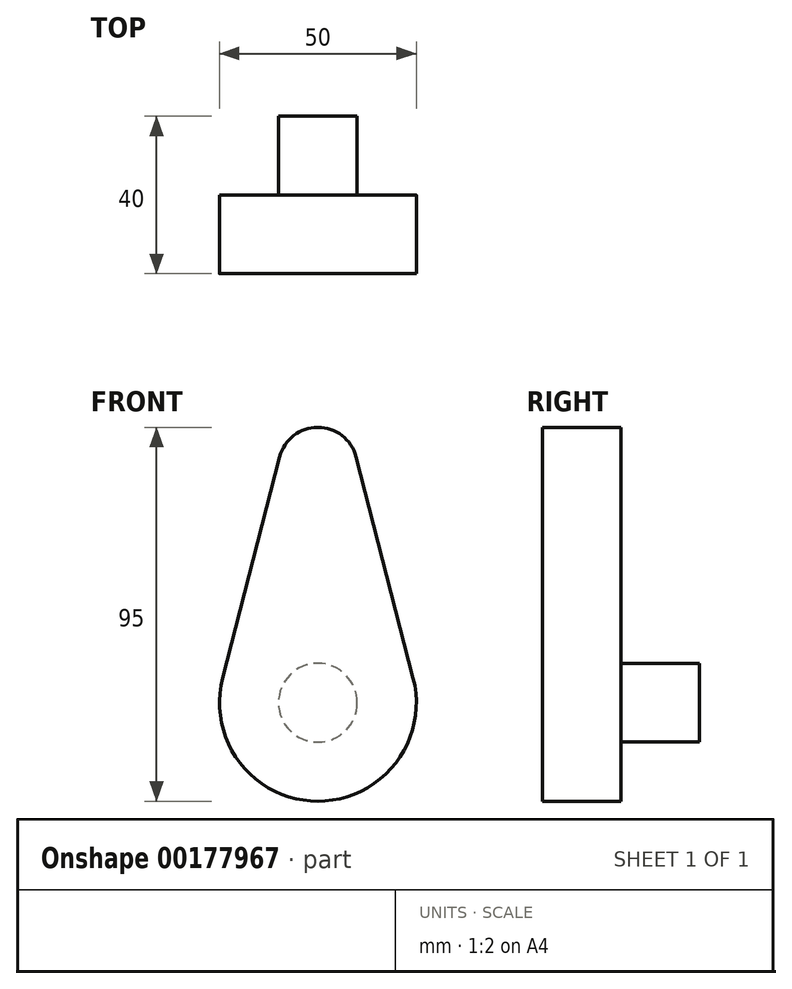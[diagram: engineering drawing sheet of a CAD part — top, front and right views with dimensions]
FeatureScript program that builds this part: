
annotation { "Feature Type Name" : "Feature", "Feature Type Description" : "" }
export const myFeature = defineFeature(function(context is Context, id is Id, definition is map)
    precondition{}
    {
        {
            var Q0;
            Q0=qCreatedBy(makeId("Front.planeOp"),FACE);
            var sketch = newSketch(context, id + "F0", { "sketchPlane" : qUnion([Q0])});
            skCircle(sketch, "E0", {"center": v(0, 0) * mm, "radius": 25 * mm});
            skCircle(sketch, "E1", {"center": v(0, 60) * mm, "radius": 10 * mm});
            skLineSegment(sketch, "E2", {"start": v(0, 60) * mm, "end": v(0, 0) * mm, "construction": true});
            skLineSegment(sketch, "E3", {"start": v(-9.68, 62.5) * mm, "end": v(-24.2, 6.25) * mm});
            skLineSegment(sketch, "E4.MirrorCS", {"start": v(9.68, 62.5) * mm, "end": v(24.2, 6.25) * mm});
            skSolve(sketch);
        }
        {
            var Q0;
            {var subQ0=sQuery(id+"F0.wireOp",EDGE,"E0");var subQ1=makeQuery(id+"F0.imprint","INTERSECT",VERTEX,{"derivedFrom":[subQ0,sQuery(id+"F0.wireOp",EDGE,"E3")]});Q0=makeQuery(id+"F0.imprint","IMPRINT",FACE,{"disambiguationData":[TD([[makeQuery(id+"F0.imprint","IMPRINT",EDGE,{"disambiguationData":[TD([[subQ1,1.0]])],"derivedFrom":subQ0}),1.0]])]});}
            var Q1;
            {var subQ0=sQuery(id+"F0.wireOp",EDGE,"E1");var subQ1=makeQuery(id+"F0.imprint","INTERSECT",VERTEX,{"derivedFrom":[subQ0,sQuery(id+"F0.wireOp",EDGE,"E3")]});Q1=makeQuery(id+"F0.imprint","IMPRINT",FACE,{"disambiguationData":[TD([[makeQuery(id+"F0.imprint","IMPRINT",EDGE,{"disambiguationData":[TD([[subQ1,1.0]])],"derivedFrom":subQ0}),1.0]])]});}
            var Q2;
            {var subQ0=sQuery(id+"F0.wireOp",EDGE,"E3");Q2=makeQuery(id+"F0.imprint","IMPRINT",FACE,{"disambiguationData":[TD([[makeQuery(id+"F0.imprint","IMPRINT",EDGE,{"derivedFrom":subQ0}),1.0]])]});}
            extrude(context, id + "F1", {"entities" : qUnion([Q0, Q1, Q2]), "depth" : 20 * mm});
        }
        {
            var Q0;
            Q0=makeQuery(id+"F1.opExtrude","CAP_FACE",FACE,{"disambiguationData":[OSD([sQuery(id+"F0.wireOp",EDGE,"E0"),sQuery(id+"F0.wireOp",EDGE,"E1"),sQuery(id+"F0.wireOp",EDGE,"E3"),sQuery(id+"F0.wireOp",EDGE,"E4.MirrorCS")])],"isStart":true});
            var sketch = newSketch(context, id + "F2", { "sketchPlane" : qUnion([Q0])});
            skCircle(sketch, "E5", {"center": v(0, 0) * mm, "radius": 10 * mm});
            skSolve(sketch);
        }
        {
            var Q0;
            Q0 = qSketchRegion(id + "F2", true);
            extrude(context, id + "F3", {"entities" : qUnion([Q0]), "operationType" : NewBodyOperationType.ADD, "depth" : 20 * mm});
        }
    });
